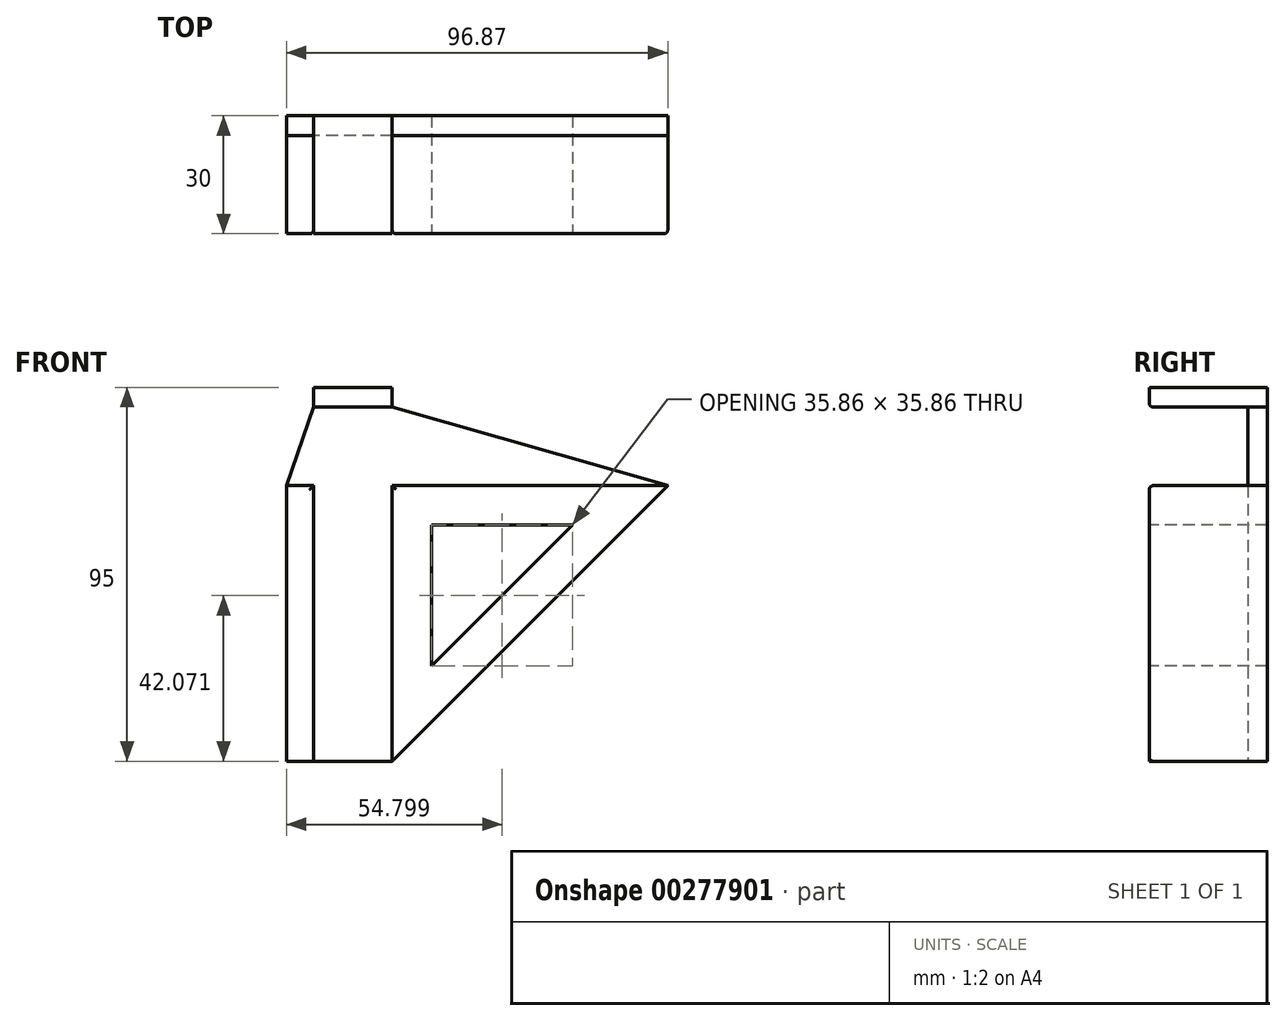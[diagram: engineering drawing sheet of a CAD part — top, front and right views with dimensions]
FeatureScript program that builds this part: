
annotation { "Feature Type Name" : "Feature", "Feature Type Description" : "" }
export const myFeature = defineFeature(function(context is Context, id is Id, definition is map)
    precondition{}
    {
        {
            var Q0;
            Q0=qCreatedBy(makeId("Front.planeOp"),FACE);
            var sketch = newSketch(context, id + "F0", { "sketchPlane" : qUnion([Q0])});
            skLineSegment(sketch, "E0", {"start": v(-16.48, 10) * mm, "end": v(0, 10) * mm, "construction": true});
            skLineSegment(sketch, "E1", {"start": v(-16.87, -10) * mm, "end": v(0, -10) * mm, "construction": true});
            skLineSegment(sketch, "E2", {"start": v(-10, 15) * mm, "end": v(-10, -80) * mm, "construction": true});
            skLineSegment(sketch, "E3", {"start": v(-16.87, -17.75) * mm, "end": v(-16.87, -17.75) * mm});
            skLineSegment(sketch, "E4", {"start": v(-16.87, -17.75) * mm, "end": v(-16.87, -80) * mm, "construction": true});
            skLineSegment(sketch, "E5", {"start": v(0, 15) * mm, "end": v(-10, 15) * mm});
            skLineSegment(sketch, "E6", {"start": v(0, -80) * mm, "end": v(-16.87, -80) * mm});
            skLineSegment(sketch, "E7", {"start": v(-10, 10) * mm, "end": v(-10, 15) * mm});
            skLineSegment(sketch, "E8.MirrorCS", {"start": v(10, 10) * mm, "end": v(10, 15) * mm});
            skLineSegment(sketch, "E9.MirrorCS", {"start": v(0, 15) * mm, "end": v(10, 15) * mm});
            skPoint(sketch, "E10.MirrorCS.end.orphan", {"position": v(16.87, -17.75) * mm});
            skPoint(sketch, "E10.MirrorCS.start.orphan", {"position": v(16.87, -80) * mm});
            skPoint(sketch, "E11.MirrorCS.start.orphan", {"position": v(0, -80) * mm});
            skPoint(sketch, "E12.MirrorCS.start.orphan", {"position": v(16.87, 0) * mm});
            skLineSegment(sketch, "E13", {"start": v(80, -10) * mm, "end": v(10, -80) * mm});
            skLineSegment(sketch, "E14", {"start": v(10, -80) * mm, "end": v(0, -80) * mm});
            skLineSegment(sketch, "E15", {"start": v(-16.87, -10) * mm, "end": v(-10, 10) * mm});
            skLineSegment(sketch, "E16", {"start": v(10, 10) * mm, "end": v(80, -10) * mm});
            skPoint(sketch, "E17.start.orphan", {"position": v(-16.87, 0) * mm});
            skLineSegment(sketch, "E18", {"start": v(-16.87, -10) * mm, "end": v(-16.87, -80) * mm});
            skSolve(sketch);
        }
        {
            var Q0;
            Q0=makeQuery(id+"F0.imprint","IMPRINT",FACE,{"disambiguationData":[TD([[makeQuery(id+"F0.imprint","IMPRINT",EDGE,{"derivedFrom":sQuery(id+"F0.wireOp",EDGE,"E5")}),1.0]])]});
            extrude(context, id + "F1", {"entities" : qUnion([Q0]), "oppositeDirection" : true, "depth" : 5 * mm});
        }
        {
            var Q0;
            Q0=makeQuery(id+"F0.imprint","IMPRINT",FACE,{"disambiguationData":[TD([[makeQuery(id+"F0.imprint","IMPRINT",EDGE,{"derivedFrom":sQuery(id+"F0.wireOp",EDGE,"E5")}),1.0]])]});
            var sketch = newSketch(context, id + "F2", { "sketchPlane" : qUnion([Q0])});
            skLineSegment(sketch, "E19.bottom", {"start": v(-10, 15) * mm, "end": v(10, 15) * mm});
            skLineSegment(sketch, "E19.top", {"start": v(-10, 10) * mm, "end": v(10, 10) * mm});
            skLineSegment(sketch, "E19.left", {"start": v(-10, 15) * mm, "end": v(-10, 10) * mm});
            skLineSegment(sketch, "E19.right", {"start": v(10, 15) * mm, "end": v(10, 10) * mm});
            skLineSegment(sketch, "E20.MirrorCS", {"start": v(80, -10) * mm, "end": v(10, -10) * mm});
            skLineSegment(sketch, "E21.MirrorCS", {"start": v(10, -10) * mm, "end": v(10, -80) * mm});
            skPoint(sketch, "E22.start.orphan", {"position": v(-16.87, -10) * mm});
            skPoint(sketch, "E23.end.orphan", {"position": v(-10, -80) * mm});
            skPoint(sketch, "E23.start.orphan", {"position": v(-10, -10) * mm});
            skLineSegment(sketch, "E24.bottom", {"start": v(-10, -10) * mm, "end": v(-16.87, -10) * mm});
            skLineSegment(sketch, "E24.top", {"start": v(-10, -80) * mm, "end": v(-16.87, -80) * mm});
            skLineSegment(sketch, "E24.left", {"start": v(-10, -10) * mm, "end": v(-10, -80) * mm});
            skLineSegment(sketch, "E24.right", {"start": v(-16.87, -10) * mm, "end": v(-16.87, -80) * mm});
            skPoint(sketch, "E25.MirrorCS.end.orphan", {"position": v(16.87, -10) * mm});
            skPoint(sketch, "E25.MirrorCS.start.orphan", {"position": v(10, -80) * mm});
            skLineSegment(sketch, "E26", {"start": v(10, -80) * mm, "end": v(80, -10) * mm});
            skSolve(sketch);
        }
        {
            var Q0;
            Q0 = qSketchRegion(id + "F2", true);
            extrude(context, id + "F3", {"entities" : qUnion([Q0]), "operationType" : NewBodyOperationType.ADD, "depth" : 25 * mm});
        }
        {
            var Q0;
            Q0=makeQuery(id+"F3.opExtrude","CAP_EDGE",EDGE,{"disambiguationData":[OSD([sQuery(id+"F2.wireOp",EDGE,"E19.top")])],"isStart":true});
            var Q1;
            Q1=makeQuery(id+"F3.opExtrude","CAP_EDGE",EDGE,{"disambiguationData":[OSD([sQuery(id+"F2.wireOp",EDGE,"E24.bottom")])],"isStart":true});
            var Q2;
            Q2=makeQuery(id+"F3.opExtrude","CAP_EDGE",EDGE,{"disambiguationData":[OSD([sQuery(id+"F2.wireOp",EDGE,"E20.MirrorCS")])],"isStart":true});
            var Q3;
            Q3=makeQuery(id+"F3.opExtrude","CAP_EDGE",EDGE,{"disambiguationData":[OSD([sQuery(id+"F2.wireOp",EDGE,"E21.MirrorCS")])],"isStart":true});
            var Q4;
            Q4=makeQuery(id+"F3.opExtrude","CAP_EDGE",EDGE,{"disambiguationData":[OSD([sQuery(id+"F2.wireOp",EDGE,"E24.left")])],"isStart":true});
            var Q5;
            Q5=makeQuery(id+"F3.opExtrude","CAP_EDGE",EDGE,{"disambiguationData":[OSD([sQuery(id+"F2.wireOp",EDGE,"E19.top")])],"isStart":false});
            var Q6;
            Q6=makeQuery(id+"F3.opExtrude","CAP_EDGE",EDGE,{"disambiguationData":[OSD([sQuery(id+"F2.wireOp",EDGE,"E20.MirrorCS")])],"isStart":false});
            var Q7;
            Q7=makeQuery(id+"F3.opExtrude","CAP_EDGE",EDGE,{"disambiguationData":[OSD([sQuery(id+"F2.wireOp",EDGE,"E21.MirrorCS")])],"isStart":false});
            var Q8;
            Q8=makeQuery(id+"F3.opExtrude","CAP_EDGE",EDGE,{"disambiguationData":[OSD([sQuery(id+"F2.wireOp",EDGE,"E24.bottom")])],"isStart":false});
            var Q9;
            Q9=makeQuery(id+"F3.opExtrude","CAP_EDGE",EDGE,{"disambiguationData":[OSD([sQuery(id+"F2.wireOp",EDGE,"E24.left")])],"isStart":false});
            fillet(context, id + "F4", {"entities" : qUnion([Q0, Q1, Q2, Q3, Q4, Q5, Q6, Q7, Q8, Q9]), "radius" : 1 * mm, "tangentPropagation" : true, "allowEdgeOverflow" : false});
        }
        {
            var Q0;
            Q0=makeQuery(id+"F3.opExtrude","CAP_FACE",FACE,{"disambiguationData":[OSD([sQuery(id+"F2.wireOp",EDGE,"E20.MirrorCS"),sQuery(id+"F2.wireOp",EDGE,"E21.MirrorCS"),sQuery(id+"F2.wireOp",EDGE,"E26")])],"isStart":false});
            var sketch = newSketch(context, id + "F5", { "sketchPlane" : qUnion([Q0])});
            skLineSegment(sketch, "E27.0", {"start": v(20, -20) * mm, "end": v(55.86, -20) * mm});
            skLineSegment(sketch, "E27.1", {"start": v(20, -55.86) * mm, "end": v(20, -20) * mm});
            skLineSegment(sketch, "E27.2", {"start": v(55.86, -20) * mm, "end": v(20, -55.86) * mm});
            skSolve(sketch);
        }
        {
            var Q0;
            Q0=makeQuery(id+"F5.imprint","IMPRINT",FACE,{"disambiguationData":[TD([[makeQuery(id+"F5.imprint","IMPRINT",EDGE,{"derivedFrom":sQuery(id+"F5.wireOp",EDGE,"E27.0")}),-1.0]])]});
            extrude(context, id + "F6", {"entities" : qUnion([Q0]), "operationType" : NewBodyOperationType.REMOVE, "endBound" : BoundingType.THROUGH_ALL, "oppositeDirection" : true, "depth" : 25 * mm});
        }
    });
